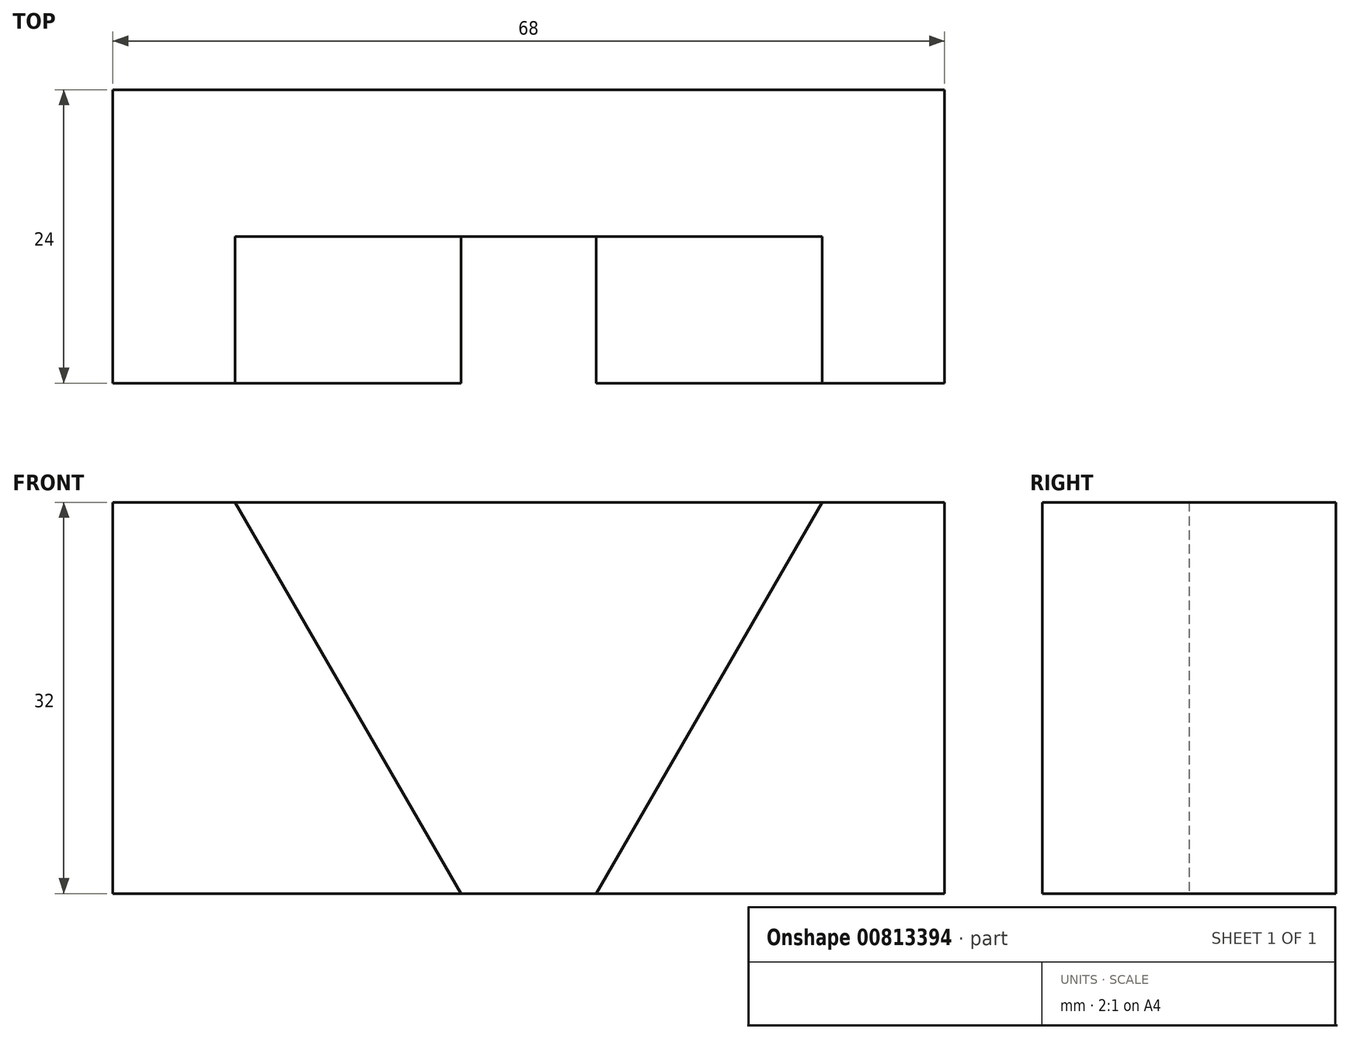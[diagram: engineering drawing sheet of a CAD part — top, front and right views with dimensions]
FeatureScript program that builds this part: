
annotation { "Feature Type Name" : "Feature", "Feature Type Description" : "" }
export const myFeature = defineFeature(function(context is Context, id is Id, definition is map)
    precondition{}
    {
        {
            var Q0;
            Q0=qCreatedBy(makeId("Front.planeOp"),FACE);
            var sketch = newSketch(context, id + "F0", { "sketchPlane" : qUnion([Q0])});
            skLineSegment(sketch, "E0.bottom", {"start": v(0, 0) * mm, "end": v(68, 0) * mm});
            skLineSegment(sketch, "E0.top", {"start": v(0, 32) * mm, "end": v(68, 32) * mm});
            skLineSegment(sketch, "E0.left", {"start": v(0, 0) * mm, "end": v(0, 32) * mm});
            skLineSegment(sketch, "E0.right", {"start": v(68, 0) * mm, "end": v(68, 32) * mm});
            skLineSegment(sketch, "E1", {"start": v(58, 32) * mm, "end": v(39.52, 0) * mm});
            skLineSegment(sketch, "E2", {"start": v(10, 32) * mm, "end": v(28.48, 0) * mm});
            skSolve(sketch);
        }
        {
            var Q0;
            Q0 = qSketchRegion(id + "F0", true);
            extrude(context, id + "F1", {"entities" : qUnion([Q0]), "oppositeDirection" : true, "depth" : 24 * mm, "offsetDistance" : 25 * mm});
        }
        {
            var Q0;
            {var subQ0=sQuery(id+"F0.wireOp",EDGE,"E1");Q0=makeQuery(id+"F0.imprint","IMPRINT",FACE,{"disambiguationData":[TD([[makeQuery(id+"F0.imprint","IMPRINT",EDGE,{"derivedFrom":subQ0}),-1.0]])]});}
            extrude(context, id + "F2", {"entities" : qUnion([Q0]), "operationType" : NewBodyOperationType.REMOVE, "oppositeDirection" : true, "depth" : 12 * mm, "offsetDistance" : 25 * mm});
        }
    });
